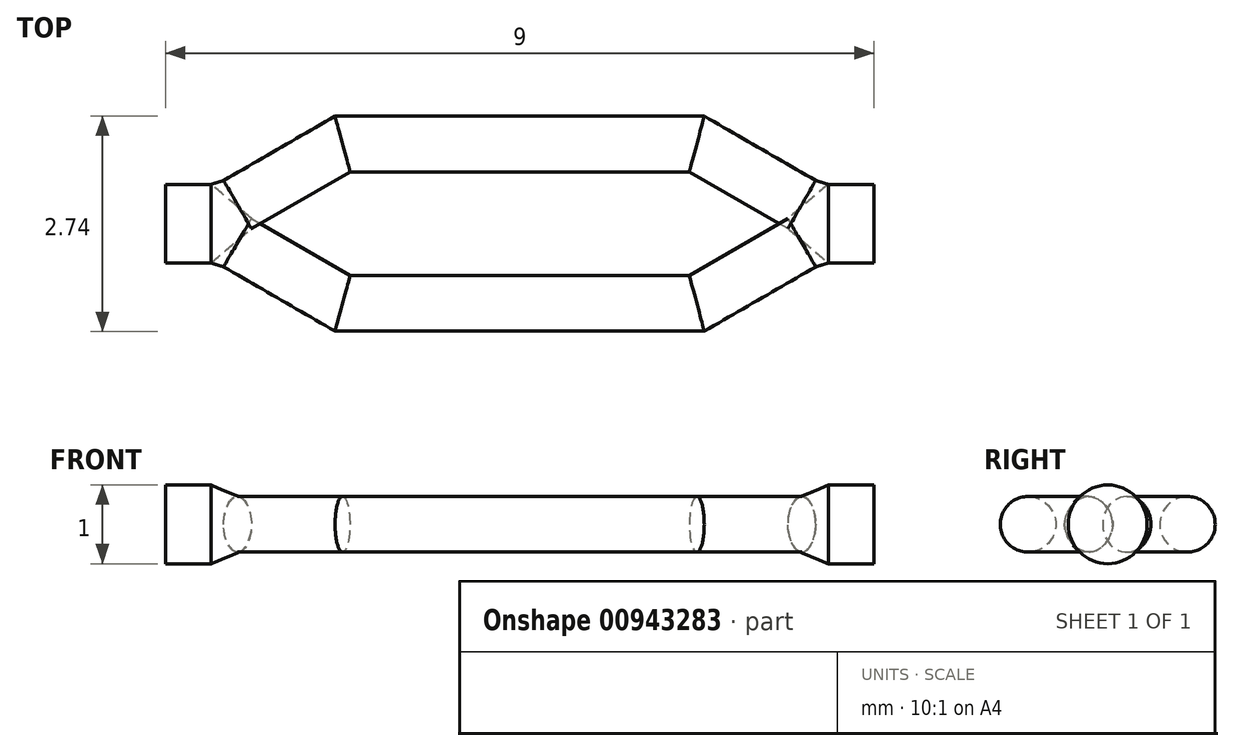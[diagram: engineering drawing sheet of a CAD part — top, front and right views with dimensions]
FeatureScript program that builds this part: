
annotation { "Feature Type Name" : "Feature", "Feature Type Description" : "" }
export const myFeature = defineFeature(function(context is Context, id is Id, definition is map)
    precondition{}
    {
        {
            var Q0;
            Q0=qCreatedBy(makeId("Top.planeOp"),FACE);
            var sketch = newSketch(context, id + "F0", { "sketchPlane" : qUnion([Q0])});
            skLineSegment(sketch, "E0.bottom", {"start": v(0, 4.5) * mm, "end": v(9, 4.5) * mm});
            skLineSegment(sketch, "E0.top", {"start": v(0, 0) * mm, "end": v(9, 0) * mm});
            skLineSegment(sketch, "E0.left", {"start": v(0, 4.5) * mm, "end": v(0, 0) * mm});
            skLineSegment(sketch, "E0.right", {"start": v(9, 4.5) * mm, "end": v(9, 0) * mm});
            skLineSegment(sketch, "E1", {"start": v(0, 2.25) * mm, "end": v(9, 2.25) * mm});
            skLineSegment(sketch, "E2", {"start": v(4.5, 4.5) * mm, "end": v(4.5, 0) * mm});
            skLineSegment(sketch, "E3", {"start": v(0, 2.25) * mm, "end": v(0.5, 2.25) * mm});
            skLineSegment(sketch, "E4", {"start": v(0.5, 2.25) * mm, "end": v(2.25, 3.26) * mm});
            skLineSegment(sketch, "E5", {"start": v(2.25, 3.26) * mm, "end": v(4.5, 3.26) * mm});
            skLineSegment(sketch, "E6", {"start": v(0, 2.25) * mm, "end": v(0.58, 2.25) * mm});
            skPoint(sketch, "E7", {"position": v(0.92, 2.5) * mm});
            skLineSegment(sketch, "E8", {"start": v(0.5, 2.25) * mm, "end": v(0.92, 2.5) * mm});
            skLineSegment(sketch, "E9", {"start": v(0.92, 2.5) * mm, "end": v(2.25, 3.26) * mm});
            skLineSegment(sketch, "E10", {"start": v(2.25, 3.26) * mm, "end": v(2.25, 2.25) * mm});
            skSolve(sketch);
        }
        {
            var Q0;
            Q0=qCreatedBy(makeId("Right.planeOp"),FACE);
            var sketch = newSketch(context, id + "F1", { "sketchPlane" : qUnion([Q0])});
            skCircle(sketch, "E11", {"center": v(2.25, 0) * mm, "radius": 0.5 * mm});
            skSolve(sketch);
        }
        {
            var Q0;
            Q0=makeQuery(id+"F1.imprint","IMPRINT",FACE,{"disambiguationData":[TD([[makeQuery(id+"F1.imprint","IMPRINT",EDGE,{"derivedFrom":sQuery(id+"F1.wireOp",EDGE,"E11")}),1.0]])]});
            var Q1;
            Q1=qSketchRegion(id+"FpUvRAgT4jxrOPf_1",true);
            var Q2;
            Q2=sQuery(id+"F0.wireOp",EDGE,"E6");
            sweep(context, id + "F2", {"profiles" : qUnion([Q0, Q1]), "path" : qUnion([Q2])});
        }
        {
            var Q0;
            Q0=sQuery(id+"F0.wireOp",EDGE,"E2");
            cPoint(context, id + "F3", {"entities" : qUnion([Q0]), "parameter" : 0.5});
        }
        {
            var Q0;
            Q0=sQuery(id+"F0.wireOp",EDGE,"E2");
            var Q1;
            Q1=qCreatedBy(id+"F3",VERTEX);
            cPlane(context, id + "F4", {"entities" : qUnion([Q0, Q1]), "cplaneType" : CPlaneType.LINE_POINT, "offset" : 25 * mm, "width" : 150 * mm, "height" : 150 * mm});
        }
        {
            var Q0;
            Q0=sQuery(id+"F0.wireOp",EDGE,"E0.bottom");
            cPoint(context, id + "F5", {"entities" : qUnion([Q0]), "parameter" : 0.5});
        }
        {
            var Q0;
            Q0=sQuery(id+"F0.wireOp",EDGE,"E0.bottom");
            var Q1;
            Q1=qCreatedBy(id+"F5",VERTEX);
            cPlane(context, id + "F6", {"entities" : qUnion([Q0, Q1]), "cplaneType" : CPlaneType.LINE_POINT, "offset" : 25 * mm, "width" : 150 * mm, "height" : 150 * mm});
        }
        {
            var Q0;
            Q0=sQuery(id+"F0.wireOp",EDGE,"E4");
            var Q1;
            Q1=sQuery(id+"F0.wireOp",VERTEX,"E7");
            var Q2;
            Q2=qBodyType(qCreatedBy(id+"F8",EDGE),BodyType.WIRE);
            cPlane(context, id + "F7", {"entities" : qUnion([Q0, Q1, Q2]), "cplaneType" : CPlaneType.LINE_POINT, "offset" : 25 * mm, "width" : 150 * mm, "height" : 150 * mm});
        }
        {
            var Q0;
            Q0=qCreatedBy(id+"F7.planeOp",FACE);
            var sketch = newSketch(context, id + "F8", { "sketchPlane" : qUnion([Q0])});
            skCircle(sketch, "E12", {"center": v(1.7, 0) * mm, "radius": 0.35 * mm});
            skSolve(sketch);
        }
        {
            var Q0;
            Q0=makeQuery(id+"F8.imprint","IMPRINT",FACE,{"disambiguationData":[TD([[makeQuery(id+"F8.imprint","IMPRINT",EDGE,{"derivedFrom":sQuery(id+"F8.wireOp",EDGE,"E12")}),1.0]])]});
            var Q1;
            Q1=sQuery(id+"F0.wireOp",EDGE,"E9");
            var Q2;
            Q2=sQuery(id+"F0.wireOp",EDGE,"E5");
            sweep(context, id + "F9", {"profiles" : qUnion([Q0]), "path" : qUnion([Q1, Q2])});
        }
        {
            var Q0;
            Q0=makeQuery(id+"F2.opSweep","CAP_FACE",FACE,{"disambiguationData":[OSD([sQuery(id+"F0.wireOp",VERTEX,"E6.end"),sQuery(id+"F1.wireOp",EDGE,"E11")])],"isStart":false});
            var Q1;
            Q1=makeQuery(id+"F9.opSweep","CAP_FACE",FACE,{"disambiguationData":[OSD([sQuery(id+"F0.wireOp",VERTEX,"E9.start"),sQuery(id+"F8.wireOp",EDGE,"E12")])],"isStart":true});
            var Q2;
            Q2=makeQuery(id+"F2.opSweep","CAP_FACE",FACE,{"disambiguationData":[OSD([sQuery(id+"F0.wireOp",VERTEX,"E6.end"),sQuery(id+"F1.wireOp",EDGE,"E11")])],"isStart":false});
            var Q3;
            Q3=makeQuery(id+"F9.opSweep","CAP_FACE",FACE,{"disambiguationData":[OSD([sQuery(id+"F0.wireOp",VERTEX,"E9.start"),sQuery(id+"F8.wireOp",EDGE,"E12")])],"isStart":true});
            var Q4;
            Q4=sQuery(id+"F0.wireOp",VERTEX,"E6.end");
            var Q5;
            Q5=sQuery(id+"F0.wireOp",VERTEX,"E7");
            loft(context, id + "F10", {"sheetProfilesArray" : [{ "sheetProfileEntities" : qUnion([Q0]) }, { "sheetProfileEntities" : qUnion([Q1]) }], "wireProfilesArray" : [{ "wireProfileEntities" : qUnion([Q2]) }, { "wireProfileEntities" : qUnion([Q3]) }], "connections" : [{ "connectionEntities" : qUnion([Q4, Q5]), "connectionEdgeQueries" : qUnion([]), "connectionEdgeParameters" : [] }]});
        }
        {
            var Q0;
            Q0=makeQuery(id+"F2.opSweep","SWEPT_BODY",BODY,{"disambiguationData":[OSD([sQuery(id+"F0.wireOp",EDGE,"E6"),sQuery(id+"F1.wireOp",EDGE,"E11")])]});
            var Q1;
            Q1=makeQuery(id+"F10.opLoft","SWEPT_BODY",BODY,{"disambiguationData":[OSD([sQuery(id+"F0.wireOp",VERTEX,"E6.end"),sQuery(id+"F0.wireOp",VERTEX,"E9.start"),sQuery(id+"F1.wireOp",EDGE,"E11"),sQuery(id+"F8.wireOp",EDGE,"E12")])]});
            var Q2;
            Q2=makeQuery(id+"F9.opSweep","SWEPT_BODY",BODY,{"disambiguationData":[OSD([sQuery(id+"F0.wireOp",EDGE,"E5"),sQuery(id+"F8.wireOp",EDGE,"E12")])]});
            var Q3;
            Q3=qCreatedBy(id+"F6.planeOp",FACE);
            mirror(context, id + "F11", {"operationType" : NewBodyOperationType.ADD, "entities" : qUnion([Q0, Q1, Q2]), "mirrorPlane" : qUnion([Q3])});
        }
        {
            var Q0;
            Q0=makeQuery(id+"F2.opSweep","SWEPT_BODY",BODY,{"disambiguationData":[OSD([sQuery(id+"F0.wireOp",EDGE,"E6"),sQuery(id+"F1.wireOp",EDGE,"E11")])]});
            var Q1;
            Q1=makeQuery(id+"F10.opLoft","SWEPT_BODY",BODY,{"disambiguationData":[OSD([sQuery(id+"F0.wireOp",VERTEX,"E6.end"),sQuery(id+"F0.wireOp",VERTEX,"E9.start"),sQuery(id+"F1.wireOp",EDGE,"E11"),sQuery(id+"F8.wireOp",EDGE,"E12")])]});
            var Q2;
            Q2=makeQuery(id+"F9.opSweep","SWEPT_BODY",BODY,{"disambiguationData":[OSD([sQuery(id+"F0.wireOp",EDGE,"E5"),sQuery(id+"F8.wireOp",EDGE,"E12")])]});
            var Q3;
            Q3=qCreatedBy(id+"F4.planeOp",FACE);
            mirror(context, id + "F12", {"entities" : qUnion([Q0, Q1, Q2]), "mirrorPlane" : qUnion([Q3])});
        }
    });
